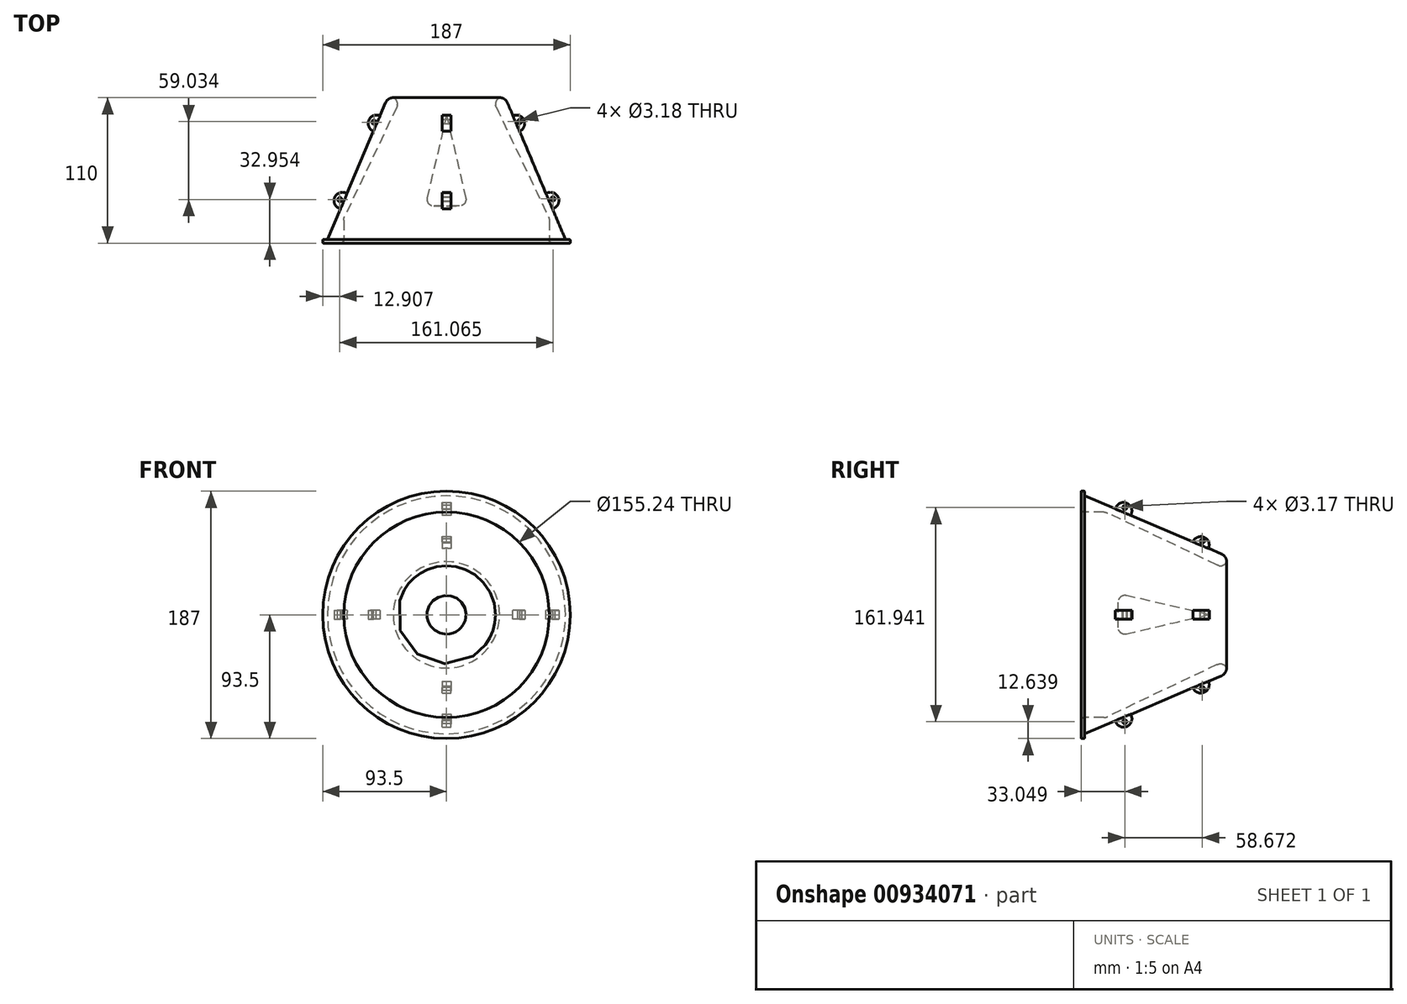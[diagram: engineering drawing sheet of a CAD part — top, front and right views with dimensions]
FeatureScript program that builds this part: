
annotation { "Feature Type Name" : "Feature", "Feature Type Description" : "" }
export const myFeature = defineFeature(function(context is Context, id is Id, definition is map)
    precondition{}
    {
        {
            var Q0;
            Q0=qCreatedBy(makeId("Top.planeOp"),FACE);
            var sketch = newSketch(context, id + "F0", { "sketchPlane" : qUnion([Q0])});
            skCircle(sketch, "E0", {"center": v(0, 0) * mm, "radius": 90 * mm});
            skSolve(sketch);
        }
        {
            var Q0;
            Q0=qCreatedBy(makeId("Top.planeOp"),FACE);
            var sketch = newSketch(context, id + "F1", { "sketchPlane" : qUnion([Q0])});
            skLineSegment(sketch, "E1", {"start": v(-77.62, 0) * mm, "end": v(-93.5, 0) * mm});
            skLineSegment(sketch, "E2", {"start": v(-93.5, 0) * mm, "end": v(-93.5, 2.72) * mm});
            skLineSegment(sketch, "E3", {"start": v(-93.5, 2.72) * mm, "end": v(-89.95, 2.72) * mm});
            skLineSegment(sketch, "E4", {"start": v(-93.5, 0) * mm, "end": v(-77.62, 0) * mm});
            skLineSegment(sketch, "E5", {"start": v(-37, 110) * mm, "end": v(-40.22, 110) * mm});
            skLineSegment(sketch, "E6", {"start": v(-46.07, 106.13) * mm, "end": v(-89.95, 2.72) * mm});
            skLineSegment(sketch, "E7", {"start": v(-77.62, 0) * mm, "end": v(-77.62, 17.26) * mm});
            skLineSegment(sketch, "E8", {"start": v(-37, 110) * mm, "end": v(-37, 105.53) * mm});
            skLineSegment(sketch, "E9", {"start": v(-37.62, 102.8) * mm, "end": v(-77, 20) * mm});
            skPoint(sketch, "E10.visualSharp", {"position": v(-37, 104.1) * mm});
            skArc(sketch, "E10.filletArc", {"start": v(-37.62, 102.8) * mm, "mid": v(-37.16, 104.13) * mm, "end": v(-37, 105.53) * mm});
            skPoint(sketch, "E11.visualSharp", {"position": v(-44.43, 110) * mm});
            skArc(sketch, "E11.filletArc", {"start": v(-40.22, 110) * mm, "mid": v(-43.73, 108.94) * mm, "end": v(-46.07, 106.13) * mm});
            skPoint(sketch, "E12.visualSharp", {"position": v(-77.62, 18.7) * mm});
            skArc(sketch, "E12.filletArc", {"start": v(-77, 20) * mm, "mid": v(-77.46, 18.66) * mm, "end": v(-77.62, 17.26) * mm});
            skLineSegment(sketch, "E13", {"start": v(0, 0) * mm, "end": v(0, 56.66) * mm});
            skSolve(sketch);
        }
        {
            var Q0;
            Q0=makeQuery(id+"F1.imprint","IMPRINT",FACE,{"disambiguationData":[TD([[makeQuery(id+"F1.imprint","IMPRINT",EDGE,{"derivedFrom":sQuery(id+"F1.wireOp",EDGE,"E2")}),-1.0]])]});
            var Q1;
            Q1=sQuery(id+"F1.wireOp",EDGE,"E13");
            revolve(context, id + "F2", {"surfaceOperationType" : NewSurfaceOperationType.NEW, "entities" : qUnion([Q0]), "axis" : qUnion([Q1]), "revolveType" : RevolveType.FULL});
        }
        {
            var Q0;
            Q0=makeQuery(id+"F2.opRevolve","SWEPT_EDGE",EDGE,{"disambiguationData":[OSD([sQuery(id+"F1.wireOp",EDGE,"E5"),sQuery(id+"F1.wireOp",EDGE,"E8")])]});
            fillet(context, id + "F3", {"entities" : qUnion([Q0]), "radius" : 5.08 * mm, "tangentPropagation" : true, "allowEdgeOverflow" : false});
        }
        {
            var Q0;
            Q0=makeQuery(id+"F2.opRevolve","SWEPT_EDGE",EDGE,{"disambiguationData":[OSD([sQuery(id+"F1.wireOp",EDGE,"E4"),sQuery(id+"F1.wireOp",EDGE,"E7")])]});
            fillet(context, id + "F4", {"entities" : qUnion([Q0]), "radius" : 2.54 * mm, "tangentPropagation" : true, "allowEdgeOverflow" : false});
        }
        {
            var Q0;
            Q0=makeQuery(id+"F2.opRevolve","SWEPT_EDGE",EDGE,{"disambiguationData":[OSD([sQuery(id+"F1.wireOp",EDGE,"E2"),sQuery(id+"F1.wireOp",EDGE,"E3")])]});
            var Q1;
            Q1=makeQuery(id+"F2.opRevolve","SWEPT_EDGE",EDGE,{"disambiguationData":[OSD([sQuery(id+"F1.wireOp",EDGE,"E2"),sQuery(id+"F1.wireOp",EDGE,"E4")])]});
            fillet(context, id + "F5", {"entities" : qUnion([Q0, Q1]), "radius" : 0.5 * mm, "tangentPropagation" : true, "allowEdgeOverflow" : false});
        }
        {
            var Q0;
            Q0=qCreatedBy(makeId("Top.planeOp"),FACE);
            var sketch = newSketch(context, id + "F6", { "sketchPlane" : qUnion([Q0])});
            skCircle(sketch, "E14", {"center": v(-78.58, 32.1) * mm, "radius": 6.35 * mm});
            skCircle(sketch, "E15", {"center": v(-52.78, 90.51) * mm, "radius": 6.35 * mm});
            skCircle(sketch, "E16.MirrorC", {"center": v(52.78, 90.51) * mm, "radius": 6.35 * mm});
            skCircle(sketch, "E17.MirrorC", {"center": v(78.58, 32.1) * mm, "radius": 6.35 * mm});
            skSolve(sketch);
        }
        {
            var Q0;
            Q0=qSketchRegion(id+"F6",true);
            extrude(context, id + "F7", {"entities" : qUnion([Q0]), "operationType" : NewBodyOperationType.ADD, "endBound" : BoundingType.SYMMETRIC, "depth" : 6.6 * mm, "offsetDistance" : 25.4 * mm});
        }
        {
            var Q0;
            Q0=makeQuery(id+"F2.opRevolve","SWEPT_BODY",BODY,{"disambiguationData":[OSD([sQuery(id+"F1.wireOp",EDGE,"E2"),sQuery(id+"F1.wireOp",EDGE,"E3"),sQuery(id+"F1.wireOp",EDGE,"E4"),sQuery(id+"F1.wireOp",EDGE,"E5"),sQuery(id+"F1.wireOp",EDGE,"E6"),sQuery(id+"F1.wireOp",EDGE,"E7"),sQuery(id+"F1.wireOp",EDGE,"E8"),sQuery(id+"F1.wireOp",EDGE,"E9"),sQuery(id+"F1.wireOp",EDGE,"E10.filletArc"),sQuery(id+"F1.wireOp",EDGE,"E11.filletArc"),sQuery(id+"F1.wireOp",EDGE,"E12.filletArc")])]});
            var Q1;
            Q1=sQuery(id+"F1.wireOp",EDGE,"E13");
            transform(context, id + "F8", {"entities" : qUnion([Q0]), "transformType" : TransformType.ROTATION, "transformAxis" : qUnion([Q1]), "angle" : 90 * degree, "oppositeDirection" : true, "makeCopy" : false});
        }
        {
            var Q0;
            Q0=qSketchRegion(id+"F6",true);
            extrude(context, id + "F9", {"entities" : qUnion([Q0]), "operationType" : NewBodyOperationType.ADD, "endBound" : BoundingType.SYMMETRIC, "depth" : 6.6 * mm, "offsetDistance" : 25.4 * mm});
        }
        {
            var Q0;
            Q0=makeQuery(id+"F9.opExtrude","CAP_FACE",FACE,{"disambiguationData":[OSD([sQuery(id+"F6.wireOp",EDGE,"E16.MirrorC")])],"isStart":true});
            var sketch = newSketch(context, id + "F10", { "sketchPlane" : qUnion([Q0])});
            skCircle(sketch, "E18", {"center": v(55.32, -91.99) * mm, "radius": 1.59 * mm});
            skCircle(sketch, "E19", {"center": v(80.47, -33.45) * mm, "radius": 1.59 * mm});
            skCircle(sketch, "E20", {"center": v(-80.6, -32.95) * mm, "radius": 1.59 * mm});
            skCircle(sketch, "E21", {"center": v(-54.84, -91.46) * mm, "radius": 1.59 * mm});
            skSolve(sketch);
        }
        {
            var Q0;
            Q0=qSketchRegion(id+"F10",true);
            var Q1;
            Q1=qConstructionFilter(qBodyType(qCreatedBy(id+"F10",EDGE),BodyType.WIRE),ConstructionObject.NO);
            extrude(context, id + "F11", {"entities" : qUnion([Q0]), "operationType" : NewBodyOperationType.REMOVE, "surfaceEntities" : qUnion([Q1]), "endBound" : BoundingType.SYMMETRIC, "depth" : 25.4 * mm, "offsetDistance" : 25.4 * mm});
        }
        {
            var Q0;
            Q0=qCreatedBy(makeId("Right.planeOp"),FACE);
            var sketch = newSketch(context, id + "F12", { "sketchPlane" : qUnion([Q0])});
            skCircle(sketch, "E22", {"center": v(33.08, 81.08) * mm, "radius": 1.59 * mm});
            skCircle(sketch, "E23", {"center": v(91.72, 55.83) * mm, "radius": 1.59 * mm});
            skCircle(sketch, "E24", {"center": v(91.67, -55.8) * mm, "radius": 1.59 * mm});
            skCircle(sketch, "E25", {"center": v(33.05, -80.86) * mm, "radius": 1.59 * mm});
            skSolve(sketch);
        }
        {
            var Q0;
            Q0=qSketchRegion(id+"F12",true);
            extrude(context, id + "F13", {"entities" : qUnion([Q0]), "operationType" : NewBodyOperationType.REMOVE, "endBound" : BoundingType.SYMMETRIC, "depth" : 25.4 * mm, "offsetDistance" : 25.4 * mm});
        }
        {
            var Q0;
            Q0=qCreatedBy(makeId("Top.planeOp"),FACE);
            var sketch = newSketch(context, id + "F14", { "sketchPlane" : qUnion([Q0])});
            skLineSegment(sketch, "E26", {"start": v(0, 28.07) * mm, "end": v(-16.03, 28.07) * mm});
            skLineSegment(sketch, "E27", {"start": v(-16.03, 28.07) * mm, "end": v(0, 96.93) * mm});
            skLineSegment(sketch, "E28", {"start": v(0, 96.93) * mm, "end": v(0, 28.07) * mm});
            skSolve(sketch);
        }
        {
            var Q0;
            Q0=makeQuery(id+"F14.imprint","IMPRINT",FACE,{"disambiguationData":[TD([[makeQuery(id+"F14.imprint","IMPRINT",EDGE,{"derivedFrom":sQuery(id+"F14.wireOp",EDGE,"E26")}),-1.0]])]});
            var Q1;
            Q1=sQuery(id+"F1.wireOp",EDGE,"E13");
            revolve(context, id + "F15", {"surfaceOperationType" : NewSurfaceOperationType.NEW, "entities" : qUnion([Q0]), "axis" : qUnion([Q1]), "revolveType" : RevolveType.FULL});
        }
        {
            var Q0;
            Q0=makeQuery(id+"F15.opRevolve","SWEPT_FACE",FACE,{"disambiguationData":[OSD([sQuery(id+"F14.wireOp",EDGE,"E27")])]});
            fillet(context, id + "F16", {"entities" : qUnion([Q0]), "radius" : 5.08 * mm, "tangentPropagation" : true, "allowEdgeOverflow" : false});
        }
    });
